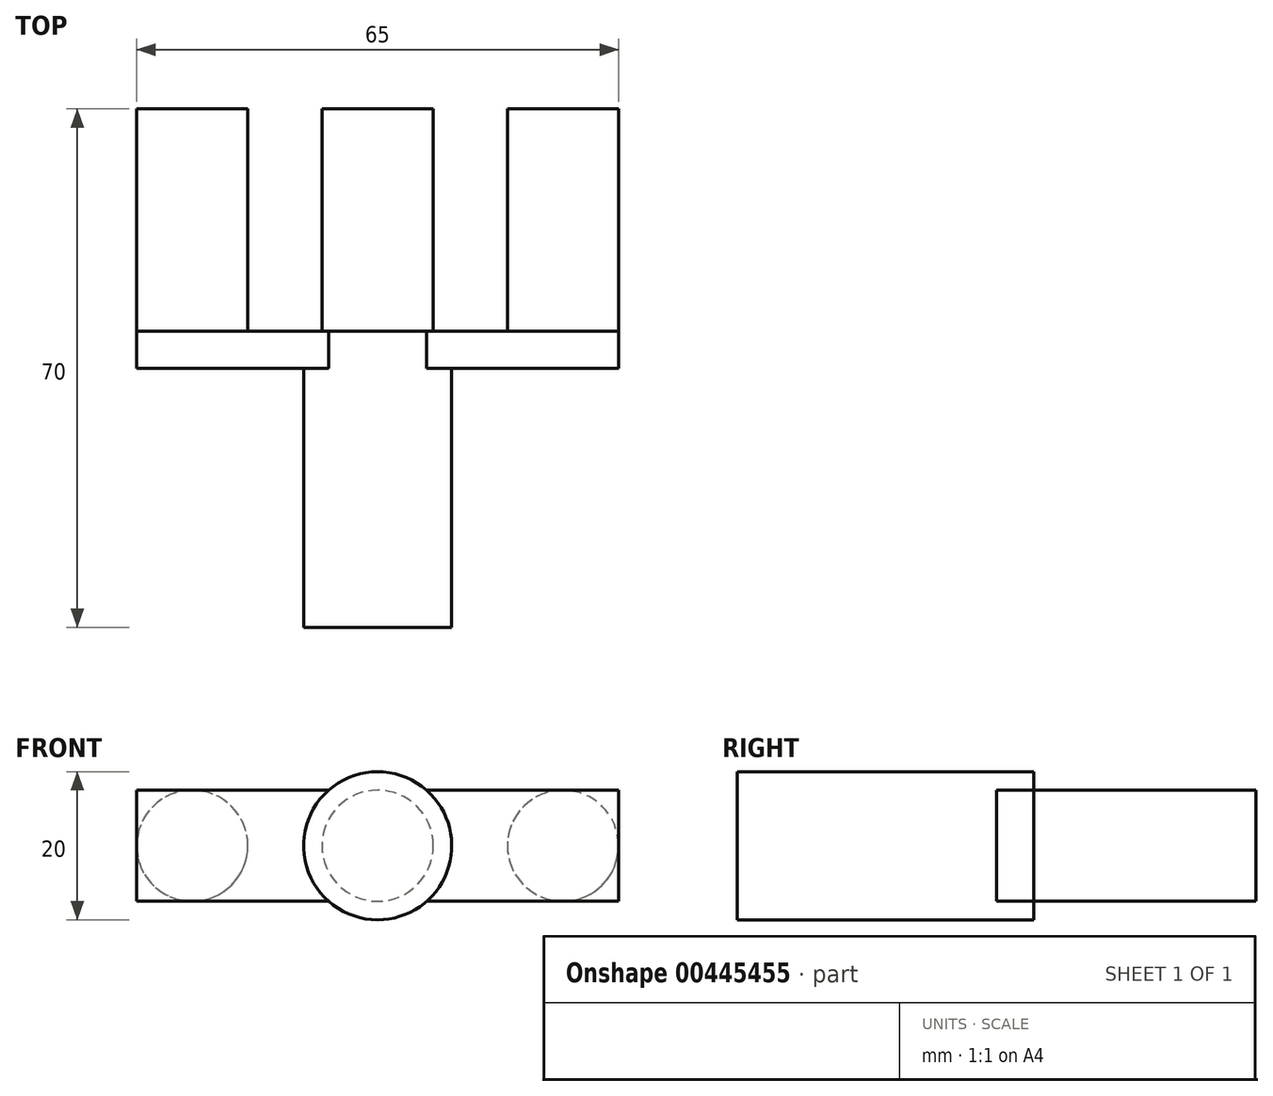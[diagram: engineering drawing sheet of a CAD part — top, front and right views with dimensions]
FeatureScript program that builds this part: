
annotation { "Feature Type Name" : "Feature", "Feature Type Description" : "" }
export const myFeature = defineFeature(function(context is Context, id is Id, definition is map)
    precondition{}
    {
        {
            var Q0;
            Q0=qCreatedBy(makeId("Front.planeOp"),FACE);
            var sketch = newSketch(context, id + "F0", { "sketchPlane" : qUnion([Q0])});
            skCircle(sketch, "E0", {"center": v(0, 0) * mm, "radius": 10 * mm});
            skSolve(sketch);
        }
        {
            var Q0;
            Q0 = qSketchRegion(id + "F0", true);
            extrude(context, id + "F1", {"entities" : qUnion([Q0]), "depth" : 40 * mm});
        }
        {
            var Q0;
            Q0=makeQuery(id+"F1.opExtrude","CAP_FACE",FACE,{"disambiguationData":[OSD([sQuery(id+"F0.wireOp",EDGE,"E0")])],"isStart":true});
            var sketch = newSketch(context, id + "F2", { "sketchPlane" : qUnion([Q0])});
            skLineSegment(sketch, "E1.bottom", {"start": v(-32.5, -7.5) * mm, "end": v(32.5, -7.5) * mm});
            skLineSegment(sketch, "E1.top", {"start": v(-32.5, 7.5) * mm, "end": v(32.5, 7.5) * mm});
            skLineSegment(sketch, "E1.left", {"start": v(-32.5, -7.5) * mm, "end": v(-32.5, 7.5) * mm});
            skLineSegment(sketch, "E1.right", {"start": v(32.5, -7.5) * mm, "end": v(32.5, 7.5) * mm});
            skPoint(sketch, "E1.middle", {"position": v(0, 0) * mm});
            skSolve(sketch);
        }
        {
            var Q0;
            Q0 = qSketchRegion(id + "F2", true);
            extrude(context, id + "F3", {"entities" : qUnion([Q0]), "operationType" : NewBodyOperationType.ADD, "oppositeDirection" : true, "depth" : 5 * mm});
        }
        {
            var Q0;
            Q0=makeQuery(id+"F3.boolean.opBoolean","MERGE",FACE,{"derivedFrom":[makeQuery(id+"F1.opExtrude","CAP_FACE",FACE,{"disambiguationData":[OSD([sQuery(id+"F0.wireOp",EDGE,"E0")])],"isStart":true}),makeQuery(id+"F3.opExtrude","CAP_FACE",FACE,{"disambiguationData":[OSD([sQuery(id+"F2.wireOp",EDGE,"E1.bottom"),sQuery(id+"F2.wireOp",EDGE,"E1.top"),sQuery(id+"F2.wireOp",EDGE,"E1.left"),sQuery(id+"F2.wireOp",EDGE,"E1.right")])],"isStart":true})]});
            var sketch = newSketch(context, id + "F4", { "sketchPlane" : qUnion([Q0])});
            skCircle(sketch, "E2", {"center": v(0, 0) * mm, "radius": 7.5 * mm});
            skCircle(sketch, "E3", {"center": v(-25, 0) * mm, "radius": 7.5 * mm});
            skCircle(sketch, "E4", {"center": v(25, 0) * mm, "radius": 7.5 * mm});
            skSolve(sketch);
        }
        {
            var Q0;
            Q0 = qSketchRegion(id + "F4", true);
            extrude(context, id + "F5", {"entities" : qUnion([Q0]), "operationType" : NewBodyOperationType.ADD, "depth" : 30 * mm});
        }
    });
